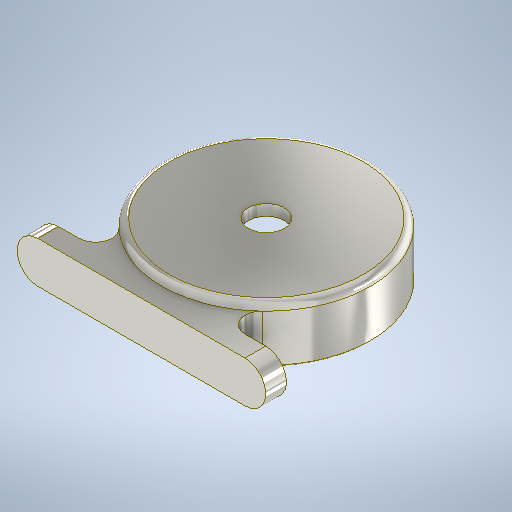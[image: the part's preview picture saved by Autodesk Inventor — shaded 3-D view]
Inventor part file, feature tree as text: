
AUTODESK INVENTOR PART (.ipt)
format: ipt  version: 2025.1 (Build 291241000, 241)  size: 372,224 bytes
history: native  units: mm
features: sketch x4, fillet x4, extrude x3, hole x2, pattern_circular x1
ambient origin geometry x8: Origin, YZ Plane, XZ Plane, XY Plane, X Axis, Y Axis, Z Axis, Center Point
bodies: Solid1 (feature_tree)
feature tree (14):
  sketch  "Sketch1"  dims[d0=15.0mm d1=12.0mm]
  extrude  "Extrusion1"  Depth=12.0mm
  extrude  "Extrusion2"  Depth=90.5mm
  extrude  "Extrusion3"  Depth=30.0mm TaperAngle=0.0deg
  fillet  "Fillet1"  Radius=40.0mm
  hole  "Hole1"  [1 undecoded]
  fillet  "Fillet3"  Radius=2.0mm
  fillet  "Fillet4"  Radius=90.5mm
  fillet  "Fillet5"  Radius=15.0mm
  hole  "Hole4"  [1 undecoded]
  pattern_circular  "Circular Pattern2"  [2 undecoded]
  sketch  "Sketch2"  dims[d2=90.5mm d3=151.0mm]
  sketch  "Sketch3"  dims[d4=180.0mm d5=30.0mm d6=0.0mm d7=40.0mm d8=0.0mm]
  sketch  "Sketch6"  dims[d9=135.0mm d10=32.0mm d11=0.0mm d12=2.0mm d13=26.0mm d14=6.0mm d15=4.0mm d16=2.0mm d17=90.0deg d18=8.0mm d19=0.0mm d20=90.5mm d33=15.0mm d41=5.0mm d42=1.0mm d43=143.0mm d44=4.134mm d45=15.0mm d46=4.0mm d47=2.0mm d48=90.0deg d49=15.0mm d50=0.0mm d51=120.0mm d52=360.0deg]
note: 4 required parameter values undecoded (feature->parameter linkage not recoverable at this tier; creation-order binding heuristic only, values carry confidence <= 0.55)
